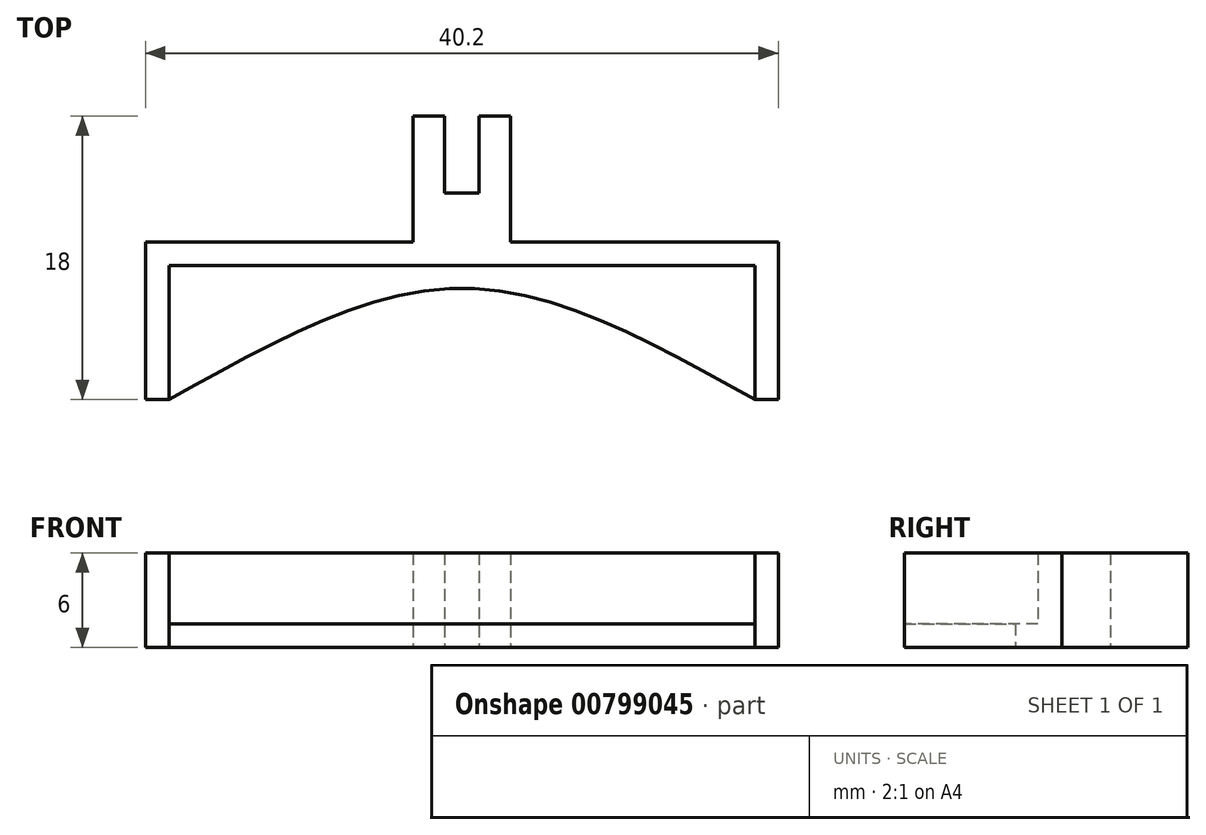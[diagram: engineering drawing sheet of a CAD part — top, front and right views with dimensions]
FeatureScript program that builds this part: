
annotation { "Feature Type Name" : "Feature", "Feature Type Description" : "" }
export const myFeature = defineFeature(function(context is Context, id is Id, definition is map)
    precondition{}
    {
        {
            var Q0;
            Q0=qCreatedBy(makeId("Top.planeOp"),FACE);
            var sketch = newSketch(context, id + "F0", { "sketchPlane" : qUnion([Q0])});
            skLineSegment(sketch, "E0", {"start": v(0, 0) * mm, "end": v(0, -8) * mm});
            skLineSegment(sketch, "E1", {"start": v(0, 0) * mm, "end": v(2, 0) * mm});
            skLineSegment(sketch, "E2", {"start": v(2, 0) * mm, "end": v(2, -4.9) * mm});
            skLineSegment(sketch, "E3", {"start": v(2, -4.9) * mm, "end": v(4.2, -4.9) * mm});
            skLineSegment(sketch, "E4", {"start": v(4.2, -4.9) * mm, "end": v(4.2, 0) * mm});
            skLineSegment(sketch, "E5", {"start": v(4.2, 0) * mm, "end": v(6.2, 0) * mm});
            skLineSegment(sketch, "E6", {"start": v(6.2, 0) * mm, "end": v(6.2, -8) * mm});
            skLineSegment(sketch, "E7", {"start": v(23.2, -8) * mm, "end": v(6.2, -8) * mm});
            skLineSegment(sketch, "E8", {"start": v(0, -8) * mm, "end": v(-17, -8) * mm});
            skLineSegment(sketch, "E9", {"start": v(-17, -8) * mm, "end": v(-17, -18) * mm});
            skLineSegment(sketch, "E10", {"start": v(-17, -18) * mm, "end": v(-15.5, -18) * mm});
            skLineSegment(sketch, "E11", {"start": v(3.1, 6.05) * mm, "end": v(3.1, -34.21) * mm, "construction": true});
            skPoint(sketch, "E11.startSnap0", {"position": v(3.1, -4.9) * mm});
            skLineSegment(sketch, "E12.MirrorCS", {"start": v(23.2, -8) * mm, "end": v(23.2, -18) * mm});
            skLineSegment(sketch, "E13.MirrorCS", {"start": v(23.2, -18) * mm, "end": v(21.7, -18) * mm});
            skLineSegment(sketch, "E14", {"start": v(-15.5, -9.5) * mm, "end": v(21.7, -9.5) * mm});
            skLineSegment(sketch, "E15", {"start": v(21.7, -18) * mm, "end": v(21.7, -9.5) * mm});
            skFitSpline(sketch, "E16", {"points": [v(-15.5, -18) * mm, v(3.1, -10.94) * mm, v(21.7, -18) * mm], "startDerivative": vector(38.2, 21.17) * mm, "endDerivative": vector(38.2, -21.17) * mm});
            skLineSegment(sketch, "E17", {"start": v(-15.5, -9.5) * mm, "end": v(-15.5, -18) * mm});
            skSolve(sketch);
        }
        {
            var Q0;
            Q0=makeQuery(id+"F0.imprint","IMPRINT",FACE,{"disambiguationData":[TD([[makeQuery(id+"F0.imprint","IMPRINT",EDGE,{"derivedFrom":sQuery(id+"F0.wireOp",EDGE,"E0")}),1.0]])]});
            extrude(context, id + "F1", {"entities" : qUnion([Q0]), "depth" : 6 * mm, "offsetDistance" : 25 * mm});
        }
        {
            var Q0;
            Q0=makeQuery(id+"F0.imprint","IMPRINT",FACE,{"disambiguationData":[TD([[makeQuery(id+"F0.imprint","IMPRINT",EDGE,{"derivedFrom":sQuery(id+"F0.wireOp",EDGE,"E14")}),-1.0]])]});
            extrude(context, id + "F2", {"entities" : qUnion([Q0]), "operationType" : NewBodyOperationType.ADD, "depth" : 1.5 * mm, "offsetDistance" : 25 * mm});
        }
    });
